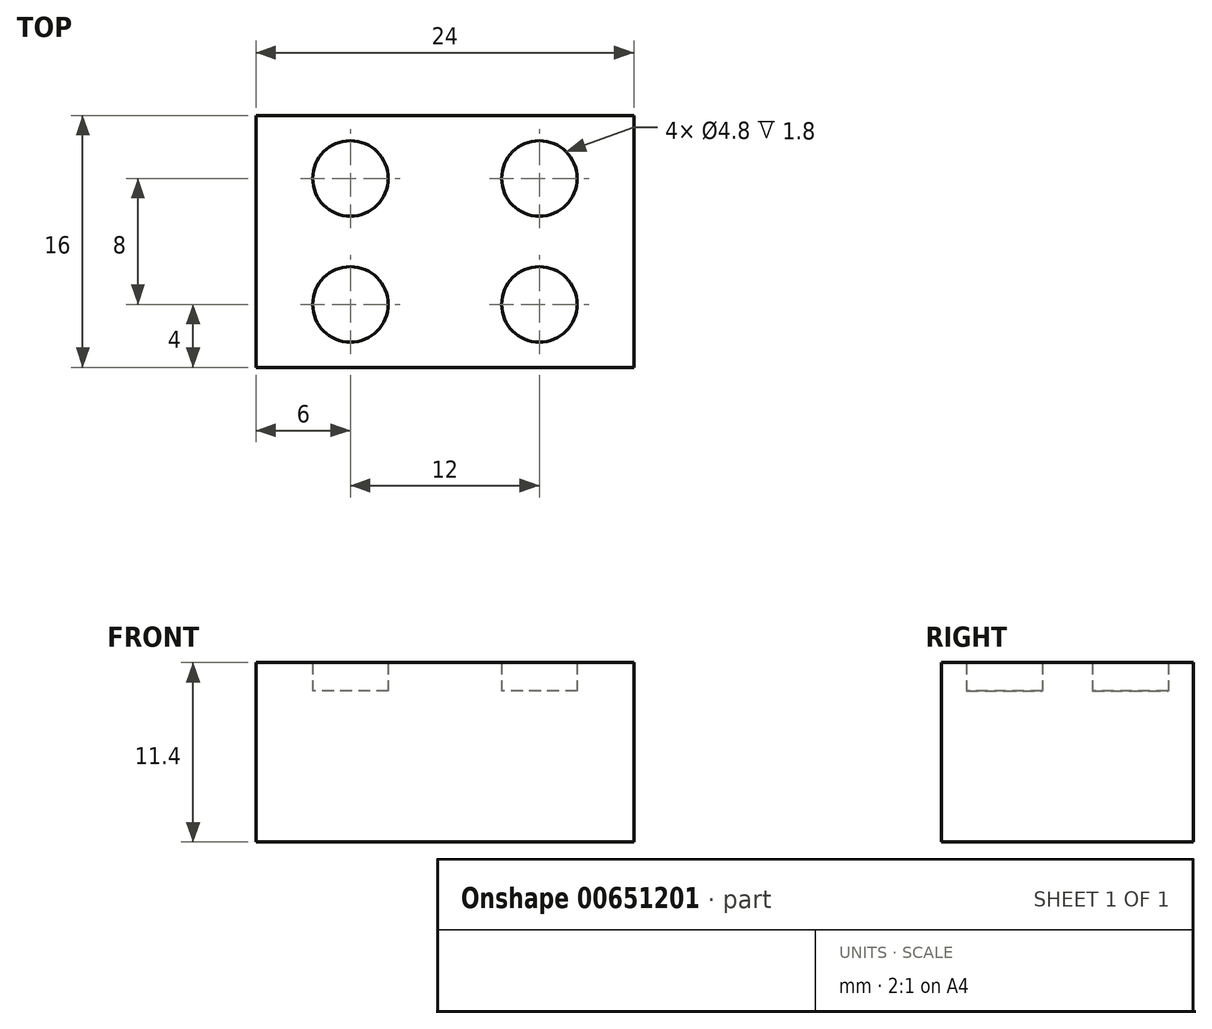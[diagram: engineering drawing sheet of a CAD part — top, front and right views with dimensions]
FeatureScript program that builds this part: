
annotation { "Feature Type Name" : "Feature", "Feature Type Description" : "" }
export const myFeature = defineFeature(function(context is Context, id is Id, definition is map)
    precondition{}
    {
        {
            var Q0;
            Q0=qCreatedBy(makeId("Top.planeOp"),FACE);
            var sketch = newSketch(context, id + "F0", { "sketchPlane" : qUnion([Q0])});
            skLineSegment(sketch, "E0.bottom", {"start": v(0, 0) * mm, "end": v(-24, 0) * mm});
            skLineSegment(sketch, "E0.top", {"start": v(0, 16) * mm, "end": v(-24, 16) * mm});
            skLineSegment(sketch, "E0.left", {"start": v(0, 0) * mm, "end": v(0, 16) * mm});
            skLineSegment(sketch, "E0.right", {"start": v(-24, 0) * mm, "end": v(-24, 16) * mm});
            skSolve(sketch);
        }
        {
            var Q0;
            Q0=makeQuery(id+"F0.imprint","IMPRINT",FACE,{"disambiguationData":[TD([[makeQuery(id+"F0.imprint","IMPRINT",EDGE,{"derivedFrom":sQuery(id+"F0.wireOp",EDGE,"E0.bottom")}),-1.0]])]});
            extrude(context, id + "F1", {"entities" : qUnion([Q0]), "depth" : 9.6 * mm, "offsetDistance" : 25.4 * mm});
        }
        {
            var Q0;
            Q0=makeQuery(id+"F1.opExtrude","CAP_FACE",FACE,{"disambiguationData":[OSD([sQuery(id+"F0.wireOp",EDGE,"E0.bottom"),sQuery(id+"F0.wireOp",EDGE,"E0.top"),sQuery(id+"F0.wireOp",EDGE,"E0.left"),sQuery(id+"F0.wireOp",EDGE,"E0.right")])],"isStart":false});
            var sketch = newSketch(context, id + "F2", { "sketchPlane" : qUnion([Q0])});
            skLineSegment(sketch, "E1", {"start": v(-24, 8) * mm, "end": v(0, 8) * mm});
            skLineSegment(sketch, "E2", {"start": v(-12, 16) * mm, "end": v(-12, 0) * mm});
            skLineSegment(sketch, "E3", {"start": v(-24, 16) * mm, "end": v(-12, 8) * mm});
            skLineSegment(sketch, "E4", {"start": v(-12, 8) * mm, "end": v(0, 16) * mm});
            skCircle(sketch, "E5", {"center": v(-18, 12) * mm, "radius": 2.4 * mm});
            skCircle(sketch, "E6", {"center": v(-6, 12) * mm, "radius": 2.4 * mm});
            skCircle(sketch, "E7.MirrorC", {"center": v(-18, 4) * mm, "radius": 2.4 * mm});
            skCircle(sketch, "E8.MirrorC", {"center": v(-6, 4) * mm, "radius": 2.4 * mm});
            skSolve(sketch);
        }
        {
            var Q0;
            {var subQ0=sQuery(id+"F2.wireOp",EDGE,"E5");var subQ1=sQuery(id+"F2.wireOp",EDGE,"E3");var subQ2=makeQuery(id+"F2.imprint","INTERSECT",VERTEX,{"disambiguationData":[OD(0.0)],"derivedFrom":[subQ1,subQ0]});Q0=makeQuery(id+"F2.imprint","IMPRINT",FACE,{"disambiguationData":[TD([[makeQuery(id+"F2.imprint","IMPRINT",EDGE,{"disambiguationData":[TD([[subQ2,-1.0]])],"derivedFrom":subQ1}),-1.0]])]});}
            var Q1;
            {var subQ0=sQuery(id+"F2.wireOp",EDGE,"E5");var subQ1=sQuery(id+"F2.wireOp",EDGE,"E3");var subQ2=makeQuery(id+"F2.imprint","INTERSECT",VERTEX,{"disambiguationData":[OD(0.0)],"derivedFrom":[subQ1,subQ0]});Q1=makeQuery(id+"F2.imprint","IMPRINT",FACE,{"disambiguationData":[TD([[makeQuery(id+"F2.imprint","IMPRINT",EDGE,{"disambiguationData":[TD([[subQ2,-1.0]])],"derivedFrom":subQ1}),1.0]])]});}
            var Q2;
            {var subQ0=sQuery(id+"F2.wireOp",EDGE,"E6");var subQ1=sQuery(id+"F2.wireOp",EDGE,"E4");var subQ2=makeQuery(id+"F2.imprint","INTERSECT",VERTEX,{"disambiguationData":[OD(0.0)],"derivedFrom":[subQ1,subQ0]});Q2=makeQuery(id+"F2.imprint","IMPRINT",FACE,{"disambiguationData":[TD([[makeQuery(id+"F2.imprint","IMPRINT",EDGE,{"disambiguationData":[TD([[subQ2,-1.0]])],"derivedFrom":subQ1}),1.0]])]});}
            var Q3;
            {var subQ0=sQuery(id+"F2.wireOp",EDGE,"E6");var subQ1=sQuery(id+"F2.wireOp",EDGE,"E4");var subQ2=makeQuery(id+"F2.imprint","INTERSECT",VERTEX,{"disambiguationData":[OD(0.0)],"derivedFrom":[subQ1,subQ0]});Q3=makeQuery(id+"F2.imprint","IMPRINT",FACE,{"disambiguationData":[TD([[makeQuery(id+"F2.imprint","IMPRINT",EDGE,{"disambiguationData":[TD([[subQ2,-1.0]])],"derivedFrom":subQ1}),-1.0]])]});}
            var Q4;
            Q4=makeQuery(id+"F2.imprint","IMPRINT",FACE,{"disambiguationData":[TD([[makeQuery(id+"F2.imprint","IMPRINT",EDGE,{"derivedFrom":sQuery(id+"F2.wireOp",EDGE,"E8.MirrorC")}),-1.0]])]});
            var Q5;
            Q5=makeQuery(id+"F2.imprint","IMPRINT",FACE,{"disambiguationData":[TD([[makeQuery(id+"F2.imprint","IMPRINT",EDGE,{"derivedFrom":sQuery(id+"F2.wireOp",EDGE,"E7.MirrorC")}),-1.0]])]});
            extrude(context, id + "F3", {"entities" : qUnion([Q0, Q1, Q2, Q3, Q4, Q5]), "operationType" : NewBodyOperationType.ADD, "depth" : 1.8 * mm, "offsetDistance" : 25.4 * mm});
        }
    });
